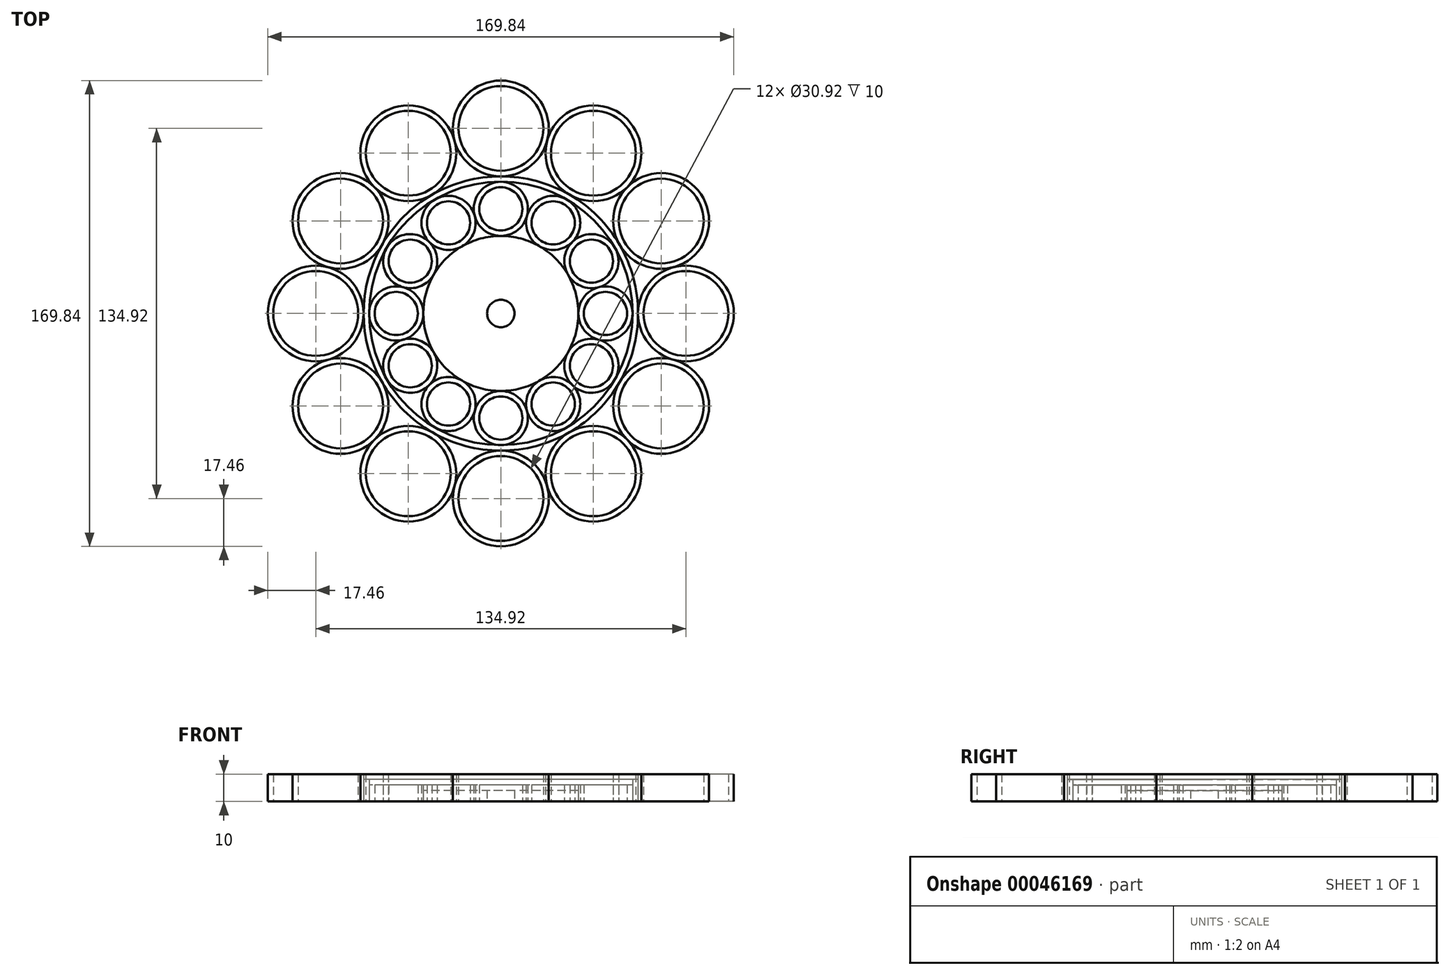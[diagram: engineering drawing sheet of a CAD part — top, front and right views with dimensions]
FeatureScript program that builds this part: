
annotation { "Feature Type Name" : "Feature", "Feature Type Description" : "" }
export const myFeature = defineFeature(function(context is Context, id is Id, definition is map)
    precondition{}
    {
        {
            var Q0;
            Q0=qCreatedBy(makeId("Top.planeOp"),FACE);
            var sketch = newSketch(context, id + "F0", { "sketchPlane" : qUnion([Q0])});
            skCircle(sketch, "E0", {"center": v(0, 0) * mm, "radius": 50 * mm});
            skCircle(sketch, "E1", {"center": v(0, 67.46) * mm, "radius": 17.46 * mm});
            skCircle(sketch, "E2", {"center": v(67.46, 0) * mm, "radius": 17.46 * mm});
            skCircle(sketch, "E3", {"center": v(0, -67.46) * mm, "radius": 17.46 * mm});
            skCircle(sketch, "E4", {"center": v(-67.46, 0) * mm, "radius": 17.46 * mm});
            skCircle(sketch, "E5", {"center": v(33.73, 58.42) * mm, "radius": 17.46 * mm});
            skCircle(sketch, "E6", {"center": v(58.42, 33.73) * mm, "radius": 17.46 * mm});
            skCircle(sketch, "E7", {"center": v(58.42, -33.73) * mm, "radius": 17.46 * mm});
            skCircle(sketch, "E8", {"center": v(33.73, -58.42) * mm, "radius": 17.46 * mm});
            skCircle(sketch, "E9", {"center": v(-33.73, -58.42) * mm, "radius": 17.46 * mm});
            skCircle(sketch, "E10", {"center": v(-58.42, -33.73) * mm, "radius": 17.46 * mm});
            skCircle(sketch, "E11", {"center": v(-58.42, 33.73) * mm, "radius": 17.46 * mm});
            skCircle(sketch, "E12", {"center": v(-33.73, 58.42) * mm, "radius": 17.46 * mm});
            skCircle(sketch, "E13", {"center": v(0, 0) * mm, "radius": 48 * mm});
            skCircle(sketch, "E14", {"center": v(0, 67.46) * mm, "radius": 15.46 * mm});
            skCircle(sketch, "E15", {"center": v(33.73, 58.42) * mm, "radius": 15.46 * mm});
            skCircle(sketch, "E16", {"center": v(58.42, 33.73) * mm, "radius": 15.46 * mm});
            skCircle(sketch, "E17", {"center": v(67.46, 0) * mm, "radius": 15.46 * mm});
            skCircle(sketch, "E18", {"center": v(0, -67.46) * mm, "radius": 15.46 * mm});
            skCircle(sketch, "E19", {"center": v(-33.73, -58.42) * mm, "radius": 15.46 * mm});
            skCircle(sketch, "E20", {"center": v(-58.42, -33.73) * mm, "radius": 15.46 * mm});
            skCircle(sketch, "E21", {"center": v(-67.46, 0) * mm, "radius": 15.46 * mm});
            skCircle(sketch, "E22", {"center": v(-58.42, 33.73) * mm, "radius": 15.46 * mm});
            skCircle(sketch, "E23", {"center": v(-33.73, 58.42) * mm, "radius": 15.46 * mm});
            skCircle(sketch, "E24", {"center": v(33.73, -58.42) * mm, "radius": 15.46 * mm});
            skCircle(sketch, "E25", {"center": v(58.42, -33.73) * mm, "radius": 15.46 * mm});
            skCircle(sketch, "E26", {"center": v(0, 38.13) * mm, "radius": 9.87 * mm});
            skCircle(sketch, "E27", {"center": v(38.13, 0) * mm, "radius": 9.87 * mm});
            skCircle(sketch, "E28", {"center": v(0, -38.13) * mm, "radius": 9.87 * mm});
            skCircle(sketch, "E29", {"center": v(-38.13, 0) * mm, "radius": 9.87 * mm});
            skCircle(sketch, "E30", {"center": v(-19.07, 33.02) * mm, "radius": 9.87 * mm});
            skCircle(sketch, "E31", {"center": v(-33.02, 19.07) * mm, "radius": 9.87 * mm});
            skCircle(sketch, "E32", {"center": v(-33.02, -19.07) * mm, "radius": 9.87 * mm});
            skCircle(sketch, "E33", {"center": v(-19.07, -33.02) * mm, "radius": 9.87 * mm});
            skCircle(sketch, "E34", {"center": v(19.07, -33.02) * mm, "radius": 9.87 * mm});
            skCircle(sketch, "E35", {"center": v(33.02, -19.07) * mm, "radius": 9.87 * mm});
            skCircle(sketch, "E36", {"center": v(33.02, 19.07) * mm, "radius": 9.87 * mm});
            skCircle(sketch, "E37", {"center": v(19.07, 33.02) * mm, "radius": 9.87 * mm});
            skCircle(sketch, "E38", {"center": v(-19.07, 33.02) * mm, "radius": 7.87 * mm});
            skCircle(sketch, "E39", {"center": v(0, 38.13) * mm, "radius": 7.87 * mm});
            skCircle(sketch, "E40", {"center": v(19.07, 33.02) * mm, "radius": 7.87 * mm});
            skCircle(sketch, "E41", {"center": v(33.02, 19.07) * mm, "radius": 7.87 * mm});
            skCircle(sketch, "E42", {"center": v(38.13, 0) * mm, "radius": 7.87 * mm});
            skCircle(sketch, "E43", {"center": v(33.02, -19.07) * mm, "radius": 7.87 * mm});
            skCircle(sketch, "E44", {"center": v(19.07, -33.02) * mm, "radius": 7.87 * mm});
            skCircle(sketch, "E45", {"center": v(0, -38.13) * mm, "radius": 7.87 * mm});
            skCircle(sketch, "E46", {"center": v(-19.07, -33.02) * mm, "radius": 7.87 * mm});
            skCircle(sketch, "E47", {"center": v(-33.02, -19.07) * mm, "radius": 7.87 * mm});
            skCircle(sketch, "E48", {"center": v(-38.13, 0) * mm, "radius": 7.87 * mm});
            skCircle(sketch, "E49", {"center": v(-33.02, 19.07) * mm, "radius": 7.87 * mm});
            skCircle(sketch, "E50", {"center": v(0, 0) * mm, "radius": 28.26 * mm});
            skCircle(sketch, "E51", {"center": v(0, 0) * mm, "radius": 5 * mm});
            skSolve(sketch);
        }
        {
            var Q0;
            Q0=makeQuery(id+"F0.imprint","IMPRINT",FACE,{"disambiguationData":[TD([[makeQuery(id+"F0.imprint","IMPRINT",EDGE,{"derivedFrom":sQuery(id+"F0.wireOp",EDGE,"E22")}),-1.0]])]});
            var Q1;
            Q1=makeQuery(id+"F0.imprint","IMPRINT",FACE,{"disambiguationData":[TD([[makeQuery(id+"F0.imprint","IMPRINT",EDGE,{"derivedFrom":sQuery(id+"F0.wireOp",EDGE,"E23")}),-1.0]])]});
            var Q2;
            Q2=makeQuery(id+"F0.imprint","IMPRINT",FACE,{"disambiguationData":[TD([[makeQuery(id+"F0.imprint","IMPRINT",EDGE,{"derivedFrom":sQuery(id+"F0.wireOp",EDGE,"E14")}),-1.0]])]});
            var Q3;
            Q3=makeQuery(id+"F0.imprint","IMPRINT",FACE,{"disambiguationData":[TD([[makeQuery(id+"F0.imprint","IMPRINT",EDGE,{"derivedFrom":sQuery(id+"F0.wireOp",EDGE,"E15")}),-1.0]])]});
            var Q4;
            Q4=makeQuery(id+"F0.imprint","IMPRINT",FACE,{"disambiguationData":[TD([[makeQuery(id+"F0.imprint","IMPRINT",EDGE,{"derivedFrom":sQuery(id+"F0.wireOp",EDGE,"E16")}),-1.0]])]});
            var Q5;
            Q5=makeQuery(id+"F0.imprint","IMPRINT",FACE,{"disambiguationData":[TD([[makeQuery(id+"F0.imprint","IMPRINT",EDGE,{"derivedFrom":sQuery(id+"F0.wireOp",EDGE,"E17")}),-1.0]])]});
            var Q6;
            Q6=makeQuery(id+"F0.imprint","IMPRINT",FACE,{"disambiguationData":[TD([[makeQuery(id+"F0.imprint","IMPRINT",EDGE,{"derivedFrom":sQuery(id+"F0.wireOp",EDGE,"E25")}),-1.0]])]});
            var Q7;
            Q7=makeQuery(id+"F0.imprint","IMPRINT",FACE,{"disambiguationData":[TD([[makeQuery(id+"F0.imprint","IMPRINT",EDGE,{"derivedFrom":sQuery(id+"F0.wireOp",EDGE,"E24")}),-1.0]])]});
            var Q8;
            Q8=makeQuery(id+"F0.imprint","IMPRINT",FACE,{"disambiguationData":[TD([[makeQuery(id+"F0.imprint","IMPRINT",EDGE,{"derivedFrom":sQuery(id+"F0.wireOp",EDGE,"E18")}),-1.0]])]});
            var Q9;
            Q9=makeQuery(id+"F0.imprint","IMPRINT",FACE,{"disambiguationData":[TD([[makeQuery(id+"F0.imprint","IMPRINT",EDGE,{"derivedFrom":sQuery(id+"F0.wireOp",EDGE,"E19")}),-1.0]])]});
            var Q10;
            Q10=makeQuery(id+"F0.imprint","IMPRINT",FACE,{"disambiguationData":[TD([[makeQuery(id+"F0.imprint","IMPRINT",EDGE,{"derivedFrom":sQuery(id+"F0.wireOp",EDGE,"E20")}),-1.0]])]});
            var Q11;
            Q11=makeQuery(id+"F0.imprint","IMPRINT",FACE,{"disambiguationData":[TD([[makeQuery(id+"F0.imprint","IMPRINT",EDGE,{"derivedFrom":sQuery(id+"F0.wireOp",EDGE,"E21")}),-1.0]])]});
            extrude(context, id + "F1", {"entities" : qUnion([Q0, Q1, Q2, Q3, Q4, Q5, Q6, Q7, Q8, Q9, Q10, Q11]), "depth" : 10 * mm});
        }
        {
            var Q0;
            {var subQ4=sQuery(id+"F0.wireOp",EDGE,"E0");var subQ8=makeQuery(id+"F0.imprint","INTERSECT",VERTEX,{"derivedFrom":[subQ4,sQuery(id+"F0.wireOp",EDGE,"E6")]});Q0=makeQuery(id+"F0.imprint","IMPRINT",FACE,{"disambiguationData":[TD([[makeQuery(id+"F0.imprint","IMPRINT",EDGE,{"disambiguationData":[TD([[subQ8,1.0]])],"derivedFrom":subQ4}),1.0]])]});}
            extrude(context, id + "F2", {"entities" : qUnion([Q0]), "depth" : 8 * mm});
        }
        {
            var Q0;
            Q0=makeQuery(id+"F0.imprint","IMPRINT",FACE,{"disambiguationData":[TD([[makeQuery(id+"F0.imprint","IMPRINT",EDGE,{"derivedFrom":sQuery(id+"F0.wireOp",EDGE,"E49")}),-1.0]])]});
            var Q1;
            Q1=makeQuery(id+"F0.imprint","IMPRINT",FACE,{"disambiguationData":[TD([[makeQuery(id+"F0.imprint","IMPRINT",EDGE,{"derivedFrom":sQuery(id+"F0.wireOp",EDGE,"E38")}),-1.0]])]});
            var Q2;
            Q2=makeQuery(id+"F0.imprint","IMPRINT",FACE,{"disambiguationData":[TD([[makeQuery(id+"F0.imprint","IMPRINT",EDGE,{"derivedFrom":sQuery(id+"F0.wireOp",EDGE,"E39")}),-1.0]])]});
            var Q3;
            Q3=makeQuery(id+"F0.imprint","IMPRINT",FACE,{"disambiguationData":[TD([[makeQuery(id+"F0.imprint","IMPRINT",EDGE,{"derivedFrom":sQuery(id+"F0.wireOp",EDGE,"E40")}),-1.0]])]});
            var Q4;
            Q4=makeQuery(id+"F0.imprint","IMPRINT",FACE,{"disambiguationData":[TD([[makeQuery(id+"F0.imprint","IMPRINT",EDGE,{"derivedFrom":sQuery(id+"F0.wireOp",EDGE,"E41")}),-1.0]])]});
            var Q5;
            Q5=makeQuery(id+"F0.imprint","IMPRINT",FACE,{"disambiguationData":[TD([[makeQuery(id+"F0.imprint","IMPRINT",EDGE,{"derivedFrom":sQuery(id+"F0.wireOp",EDGE,"E42")}),-1.0]])]});
            var Q6;
            Q6=makeQuery(id+"F0.imprint","IMPRINT",FACE,{"disambiguationData":[TD([[makeQuery(id+"F0.imprint","IMPRINT",EDGE,{"derivedFrom":sQuery(id+"F0.wireOp",EDGE,"E43")}),-1.0]])]});
            var Q7;
            Q7=makeQuery(id+"F0.imprint","IMPRINT",FACE,{"disambiguationData":[TD([[makeQuery(id+"F0.imprint","IMPRINT",EDGE,{"derivedFrom":sQuery(id+"F0.wireOp",EDGE,"E44")}),-1.0]])]});
            var Q8;
            Q8=makeQuery(id+"F0.imprint","IMPRINT",FACE,{"disambiguationData":[TD([[makeQuery(id+"F0.imprint","IMPRINT",EDGE,{"derivedFrom":sQuery(id+"F0.wireOp",EDGE,"E45")}),-1.0]])]});
            var Q9;
            Q9=makeQuery(id+"F0.imprint","IMPRINT",FACE,{"disambiguationData":[TD([[makeQuery(id+"F0.imprint","IMPRINT",EDGE,{"derivedFrom":sQuery(id+"F0.wireOp",EDGE,"E46")}),-1.0]])]});
            var Q10;
            Q10=makeQuery(id+"F0.imprint","IMPRINT",FACE,{"disambiguationData":[TD([[makeQuery(id+"F0.imprint","IMPRINT",EDGE,{"derivedFrom":sQuery(id+"F0.wireOp",EDGE,"E47")}),-1.0]])]});
            var Q11;
            Q11=makeQuery(id+"F0.imprint","IMPRINT",FACE,{"disambiguationData":[TD([[makeQuery(id+"F0.imprint","IMPRINT",EDGE,{"derivedFrom":sQuery(id+"F0.wireOp",EDGE,"E48")}),-1.0]])]});
            extrude(context, id + "F3", {"entities" : qUnion([Q0, Q1, Q2, Q3, Q4, Q5, Q6, Q7, Q8, Q9, Q10, Q11]), "operationType" : NewBodyOperationType.ADD, "depth" : 6 * mm});
        }
        {
            var Q0;
            Q0=makeQuery(id+"F0.imprint","IMPRINT",FACE,{"disambiguationData":[TD([[makeQuery(id+"F0.imprint","IMPRINT",EDGE,{"derivedFrom":sQuery(id+"F0.wireOp",EDGE,"E51")}),-1.0]])]});
            extrude(context, id + "F4", {"entities" : qUnion([Q0]), "depth" : 4 * mm});
        }
    });
